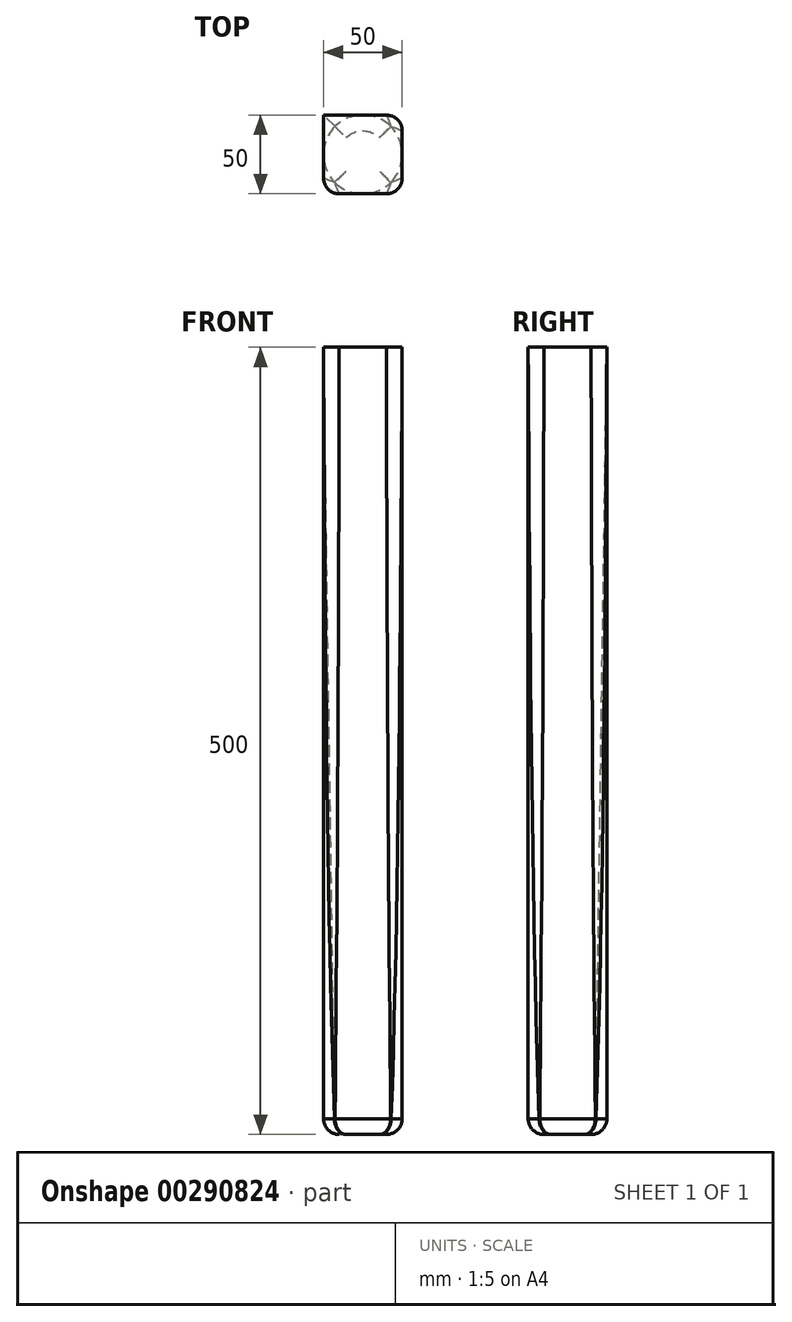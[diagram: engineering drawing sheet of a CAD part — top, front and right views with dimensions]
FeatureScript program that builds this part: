
annotation { "Feature Type Name" : "Feature", "Feature Type Description" : "" }
export const myFeature = defineFeature(function(context is Context, id is Id, definition is map)
    precondition{}
    {
        {
            var Q0;
            Q0=qCreatedBy(makeId("Top.planeOp"),FACE);
            var sketch = newSketch(context, id + "F0", { "sketchPlane" : qUnion([Q0])});
            skCircle(sketch, "E0", {"center": v(0, 0) * mm, "radius": 25 * mm});
            skSolve(sketch);
        }
        {
            var Q0;
            Q0=qCreatedBy(makeId("Top.planeOp"),FACE);
            cPlane(context, id + "F1", {"entities" : qUnion([Q0]), "cplaneType" : CPlaneType.OFFSET, "offset" : 500 * mm, "width" : 150 * mm, "height" : 150 * mm});
        }
        {
            var Q0;
            Q0=qCreatedBy(id+"F1.planeOp",FACE);
            var sketch = newSketch(context, id + "F2", { "sketchPlane" : qUnion([Q0])});
            skLineSegment(sketch, "E1.bottom", {"start": v(25, 25) * mm, "end": v(-25, 25) * mm});
            skLineSegment(sketch, "E1.top", {"start": v(25, -25) * mm, "end": v(-25, -25) * mm});
            skLineSegment(sketch, "E1.left", {"start": v(25, 25) * mm, "end": v(25, -25) * mm});
            skLineSegment(sketch, "E1.right", {"start": v(-25, 25) * mm, "end": v(-25, -25) * mm});
            skPoint(sketch, "E1.middle", {"position": v(0, 0) * mm});
            skSolve(sketch);
        }
        {
            var Q0;
            Q0=makeQuery(id+"F0.imprint","IMPRINT",FACE,{"disambiguationData":[TD([[makeQuery(id+"F0.imprint","IMPRINT",EDGE,{"derivedFrom":sQuery(id+"F0.wireOp",EDGE,"E0")}),1.0]])]});
            var Q1;
            Q1=makeQuery(id+"F2.imprint","IMPRINT",FACE,{"disambiguationData":[TD([[makeQuery(id+"F2.imprint","IMPRINT",EDGE,{"derivedFrom":sQuery(id+"F2.wireOp",EDGE,"E1.bottom")}),1.0]])]});
            loft(context, id + "F3", {"sheetProfilesArray" : [{ "sheetProfileEntities" : qUnion([Q0]) }, { "sheetProfileEntities" : qUnion([Q1]) }]});
        }
        {
            var Q0;
            Q0=makeQuery(id+"F3.opLoft","SWEPT_EDGE",EDGE,{"disambiguationData":[OSD([sQuery(id+"F0.wireOp",EDGE,"E0"),sQuery(id+"F2.wireOp",EDGE,"E1.top"),sQuery(id+"F2.wireOp",EDGE,"E1.left"),sQuery(id+"F2.wireOp",EDGE,"E1.right")])]});
            var Q1;
            Q1=makeQuery(id+"F3.opLoft","SWEPT_EDGE",EDGE,{"disambiguationData":[OSD([sQuery(id+"F0.wireOp",EDGE,"E0"),sQuery(id+"F2.wireOp",EDGE,"E1.bottom"),sQuery(id+"F2.wireOp",EDGE,"E1.top"),sQuery(id+"F2.wireOp",EDGE,"E1.right")])]});
            var Q2;
            Q2=makeQuery(id+"F3.opLoft","SWEPT_EDGE",EDGE,{"disambiguationData":[OSD([sQuery(id+"F0.wireOp",EDGE,"E0"),sQuery(id+"F2.wireOp",EDGE,"E1.bottom"),sQuery(id+"F2.wireOp",EDGE,"E1.left"),sQuery(id+"F2.wireOp",EDGE,"E1.right")])]});
            var Q3;
            Q3=makeQuery(id+"F3.opLoft","SWEPT_EDGE",EDGE,{"disambiguationData":[OSD([sQuery(id+"F2.wireOp",EDGE,"E1.bottom"),sQuery(id+"F2.wireOp",EDGE,"E1.left")])]});
            var Q4;
            Q4=makeQuery(id+"F3.opLoft","MID_CAP_EDGE",EDGE,{"disambiguationData":[OSD([sQuery(id+"F0.wireOp",EDGE,"E0"),sQuery(id+"F2.wireOp",EDGE,"E1.bottom"),sQuery(id+"F2.wireOp",EDGE,"E1.top"),sQuery(id+"F2.wireOp",EDGE,"E1.right")])],"capPos":0.0});
            var Q5;
            Q5=makeQuery(id+"F3.opLoft","MID_CAP_EDGE",EDGE,{"disambiguationData":[OSD([sQuery(id+"F0.wireOp",EDGE,"E0"),sQuery(id+"F2.wireOp",EDGE,"E1.bottom"),sQuery(id+"F2.wireOp",EDGE,"E1.top"),sQuery(id+"F2.wireOp",EDGE,"E1.left"),sQuery(id+"F2.wireOp",EDGE,"E1.right")])],"capPos":0.0});
            var Q6;
            Q6=makeQuery(id+"F3.opLoft","MID_CAP_EDGE",EDGE,{"disambiguationData":[OSD([sQuery(id+"F0.wireOp",EDGE,"E0"),sQuery(id+"F2.wireOp",EDGE,"E1.bottom"),sQuery(id+"F2.wireOp",EDGE,"E1.left")])],"capPos":0.0});
            var Q7;
            Q7=makeQuery(id+"F3.opLoft","MID_CAP_EDGE",EDGE,{"disambiguationData":[OSD([sQuery(id+"F0.wireOp",EDGE,"E0"),sQuery(id+"F2.wireOp",EDGE,"E1.bottom"),sQuery(id+"F2.wireOp",EDGE,"E1.left"),sQuery(id+"F2.wireOp",EDGE,"E1.right")])],"capPos":0.0});
            fillet(context, id + "F4", {"entities" : qUnion([Q0, Q1, Q2, Q3, Q4, Q5, Q6, Q7]), "radius" : 10 * mm, "tangentPropagation" : true, "allowEdgeOverflow" : false});
        }
    });
